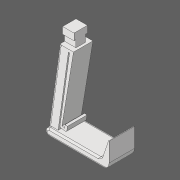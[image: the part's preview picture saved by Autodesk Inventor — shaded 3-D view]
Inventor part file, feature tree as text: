
AUTODESK INVENTOR PART (.ipt)
format: ipt  version: 2020 (Build 240168000, 168)  size: 254,464 bytes
history: native  units: in
note: dims shown in document units (in); Inventor stores cm internally (conversion verified against a paired STEP export)
features: fillet x5, other x3, extrude x3
ambient origin geometry x8: Origin, YZ Plane, XZ Plane, XY Plane, X Axis, Y Axis, Z Axis, Center Point
bodies: Solid1 (feature_tree)
feature tree (11):
  other  "Neck Start Plane"
  other  "Arm Profile"
  extrude  "Main Arm"  Depth=0.0039in
  extrude  "Pincher"  Depth=1.0386in
  extrude  "Neck"  Depth=0.6299in
  fillet  "Spring Hook Fillet"  Radius=0.1181in
  fillet  "Spring Attachment Fillet"  [1 undecoded]
  fillet  "Soft Edges"  Radius=0.1941in
  fillet  "Pincher Fillet 1"  Radius=0.0197in
  fillet  "Pincher Fillet 2"  Radius=0.0394in
  other  "Neck Sketch"
note: 1 required parameter value undecoded (feature->parameter linkage not recoverable at this tier; creation-order binding heuristic only, values carry confidence <= 0.55)
